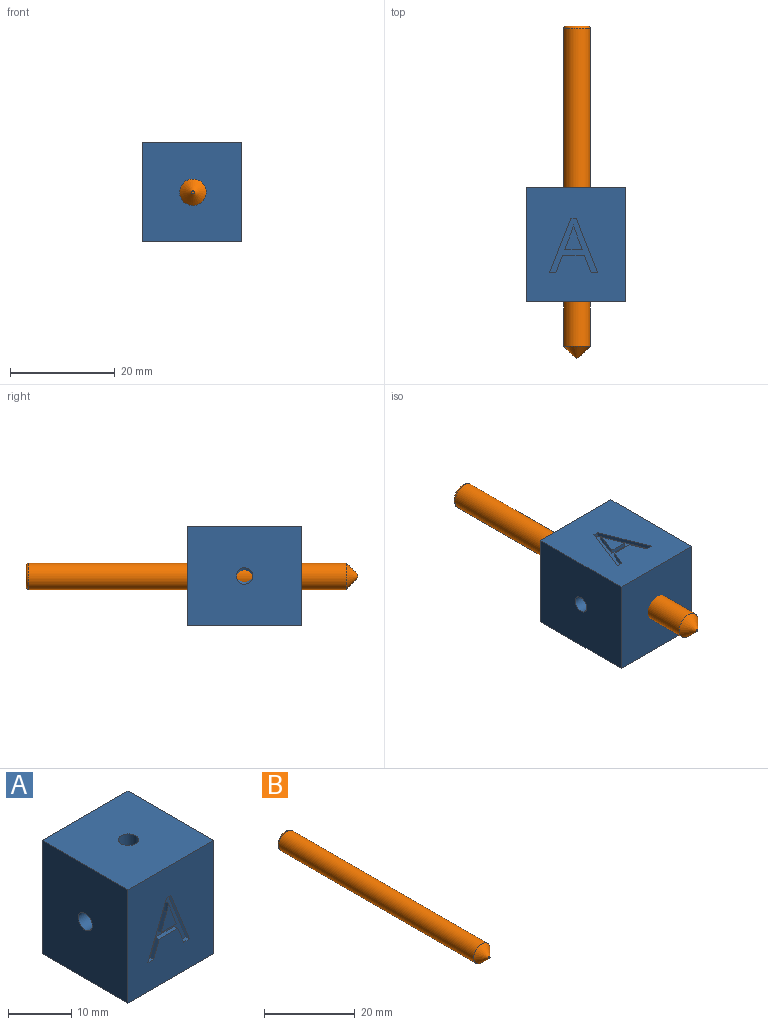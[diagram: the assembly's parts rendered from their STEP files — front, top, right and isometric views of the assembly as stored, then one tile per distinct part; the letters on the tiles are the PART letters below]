
ASSEMBLY  parts=2 mates=1
PART A: 57 faces, bbox 19.1x19.1x21.9 mm
  f0: plane 21.86x19.05mm, normal (1,0,0), area 383.1mm2, adj f1,f2,f3,f5,f41,f42,f43,f44
  f1: plane 21.86x19.05mm, normal (0,1,0), area 362.4mm2, adj f0,f3,f4,f5,f24,f25,f26,f27
  f2: plane 21.86x19.05mm, normal (0,-1,0), area 381.1mm2, adj f0,f3,f4,f5,f9,f10,f11,f12
  f3: plane 19.05x19.05mm, normal (0,0,1), area 355mm2, adj f0,f1,f2,f4,f6
  f4: plane 21.86x19.05mm, normal (-1,0,0), area 408.6mm2, adj f1,f2,f3,f5,f7
  f5: plane 19.05x19.05mm, normal (0,0,-1), area 355mm2, adj f0,f1,f2,f4,f6
  f6: cylinder r=1.59mm len=21.86mm, axis (0,0,1), area 218.1mm2, adj f3,f5
  f7: cylinder r=1.59mm len=7.11mm, axis (-1,0,0), area 70.9mm2, adj f4,f8
  f8: cone r=0mm half-angle=59deg, axis (-1,0,0), area 9.2mm2, adj f7
  f9: plane 1.25x0.79mm, normal (0,0,1), area 1mm2, adj f2,f10,f21,f22
  f10: plane 10.44x4.09mm, normal (-0.93,0,-0.36), area 8.9mm2, adj f2,f9,f11,f22
  f11: plane 1.02x0.79mm, normal (0,0,-1), area 0.8mm2, adj f2,f10,f12,f22
  f12: plane 10.44x4.11mm, normal (0.93,0,-0.37), area 8.9mm2, adj f2,f11,f13,f22
  f13: plane 1.22x0.79mm, normal (0,0,1), area 1mm2, adj f2,f12,f14,f22
  f14: plane 3.31x1.28mm, normal (-0.93,0,0.36), area 2.8mm2, adj f2,f13,f15,f22
  f15: plane 4.17x0.79mm, normal (0,0,1), area 3.3mm2, adj f2,f14,f21,f22
  f16: plane 3.36x0.79mm, normal (0,0,-1), area 2.7mm2, adj f17,f20,f22,f23
  f17: plane 3.22x1.22mm, normal (-0.94,0,0.35), area 2.7mm2, adj f16,f18,f22,f23
  f18: extruded ~1.5x0.79mm, area 1.2mm2, adj f17,f19,f22,f23
  f19: extruded ~1.5x0.79mm, area 1.3mm2, adj f18,f20,f22,f23
  f20: plane 3.22x1.21mm, normal (0.94,0,0.35), area 2.7mm2, adj f16,f19,f22,f23
  f21: plane 3.31x1.29mm, normal (0.93,0,0.36), area 2.8mm2, adj f2,f9,f15,f22
  f22: plane 10.44x9.22mm, normal (0,-1,0), area 27.8mm2, adj f9,f10,f11,f12,f13,f14,f15,f16
  f23: plane 4.72x3.36mm, normal (0,-1,0), area 7.6mm2, adj f16,f17,f18,f19,f20
  f24: extruded ~4.41x3.43mm, area 5.1mm2, adj f1,f25,f38,f39
  f25: plane 3.06x0.79mm, normal (0,0,-1), area 2.4mm2, adj f1,f24,f26,f39
  f26: plane 11.78x0.79mm, normal (-1,0,0), area 9.4mm2, adj f1,f25,f27,f39
  f27: plane 1.37x0.79mm, normal (0,0,1), area 1.1mm2, adj f1,f26,f28,f39
  f28: plane 4.63x0.79mm, normal (1,0,0), area 3.7mm2, adj f1,f27,f29,f39
  f29: plane 1.39x0.79mm, normal (0,0,1), area 1.1mm2, adj f1,f28,f30,f39
  f30: extruded ~3.49x0.96mm, area 2.9mm2, adj f1,f29,f38,f39
  f31: plane 4.79x0.79mm, normal (1,0,0), area 3.8mm2, adj f32,f37,f39,f40
  f32: plane 1.53x0.79mm, normal (0,0,1), area 1.2mm2, adj f31,f33,f39,f40
  f33: extruded ~2.39x0.79mm, area 2mm2, adj f32,f34,f39,f40
  f34: extruded ~1.74x0.79mm, area 1.6mm2, adj f33,f35,f39,f40
  f35: extruded ~1.89x0.81mm, area 1.7mm2, adj f34,f36,f39,f40
  f36: extruded ~2.63x0.79mm, area 2.2mm2, adj f35,f37,f39,f40
  f37: plane 1.24x0.79mm, normal (0,0,-1), area 1mm2, adj f31,f36,f39,f40
  f38: extruded ~2.75x1.22mm, area 2.5mm2, adj f1,f24,f30,f39
  f39: plane 11.78x7.47mm, normal (0,1,0), area 34.2mm2, adj f24,f25,f26,f27,f28,f29,f30,f31
  f40: plane 4.79x4.68mm, normal (0,1,0), area 19.9mm2, adj f31,f32,f33,f34,f35,f36,f37
  f41: plane 10.07x0.79mm, normal (0,-1,0), area 8mm2, adj f0,f42,f55,f56
  f42: plane 1.1x0.79mm, normal (0,0,-1), area 0.9mm2, adj f0,f41,f43,f56
  f43: plane 5.78x0.79mm, normal (0,1,0), area 4.6mm2, adj f0,f42,f44,f56
  f44: extruded ~1.44x0.79mm, area 1.1mm2, adj f0,f43,f45,f56
  f45: extruded ~1.19x0.79mm, area 0.9mm2, adj f0,f44,f46,f56
  f46: plane 0.79x0.06mm, normal (0,0,-1), area 0mm2, adj f0,f45,f47,f56
  f47: plane 8.41x5.49mm, normal (0,-0.84,-0.55), area 8mm2, adj f0,f46,f48,f56
  f48: plane 1.32x0.79mm, normal (0,0,-1), area 1mm2, adj f0,f47,f49,f56
  f49: plane 10.07x0.79mm, normal (0,1,0), area 8mm2, adj f0,f48,f50,f56
  f50: plane 1.08x0.79mm, normal (0,0,1), area 0.9mm2, adj f0,f49,f51,f56
  f51: plane 5.72x0.79mm, normal (0,-1,0), area 4.5mm2, adj f0,f50,f52,f56
  f52: extruded ~2.73x0.79mm, area 2.2mm2, adj f0,f51,f53,f56
  f53: plane 0.79x0.06mm, normal (0,0,1), area 0mm2, adj f0,f52,f54,f56
  f54: plane 8.45x5.5mm, normal (0,0.84,0.55), area 8mm2, adj f0,f53,f55,f56
  f55: plane 1.34x0.79mm, normal (0,0,1), area 1.1mm2, adj f0,f41,f54,f56
  f56: plane 10.07x7.86mm, normal (1,0,0), area 33.4mm2, adj f41,f42,f43,f44,f45,f46,f47,f48
PART B: 5 faces, bbox 5.5x63.5x5.5 mm
  f0: cylinder r=2.54mm len=60.71mm, axis (0,1,0), area 968.8mm2, adj f3,f4
  f1: plane 0.51x0.51mm, normal (0,-1,0), area 0.2mm2, adj f4
  f2: plane 4.06x4.06mm, normal (0,1,0), area 13mm2, adj f3
  f3: torus R=2.03mm, axis (0,-1,0), area 11.8mm2, adj f0,f2
  f4: cone r=0.25mm half-angle=45deg, axis (0,1,0), area 28.4mm2, adj f0,f1
PLACE A rot(axis=(-1,0,0),90deg) t=(421.45,50.71,-32.21)mm
PLACE B t=(70.75,-58.05,-28.33)mm
MATE fastened A.f6 <-> B.f0  axis (0,1,0) through (59.16,-88.91,-22.73)mm
